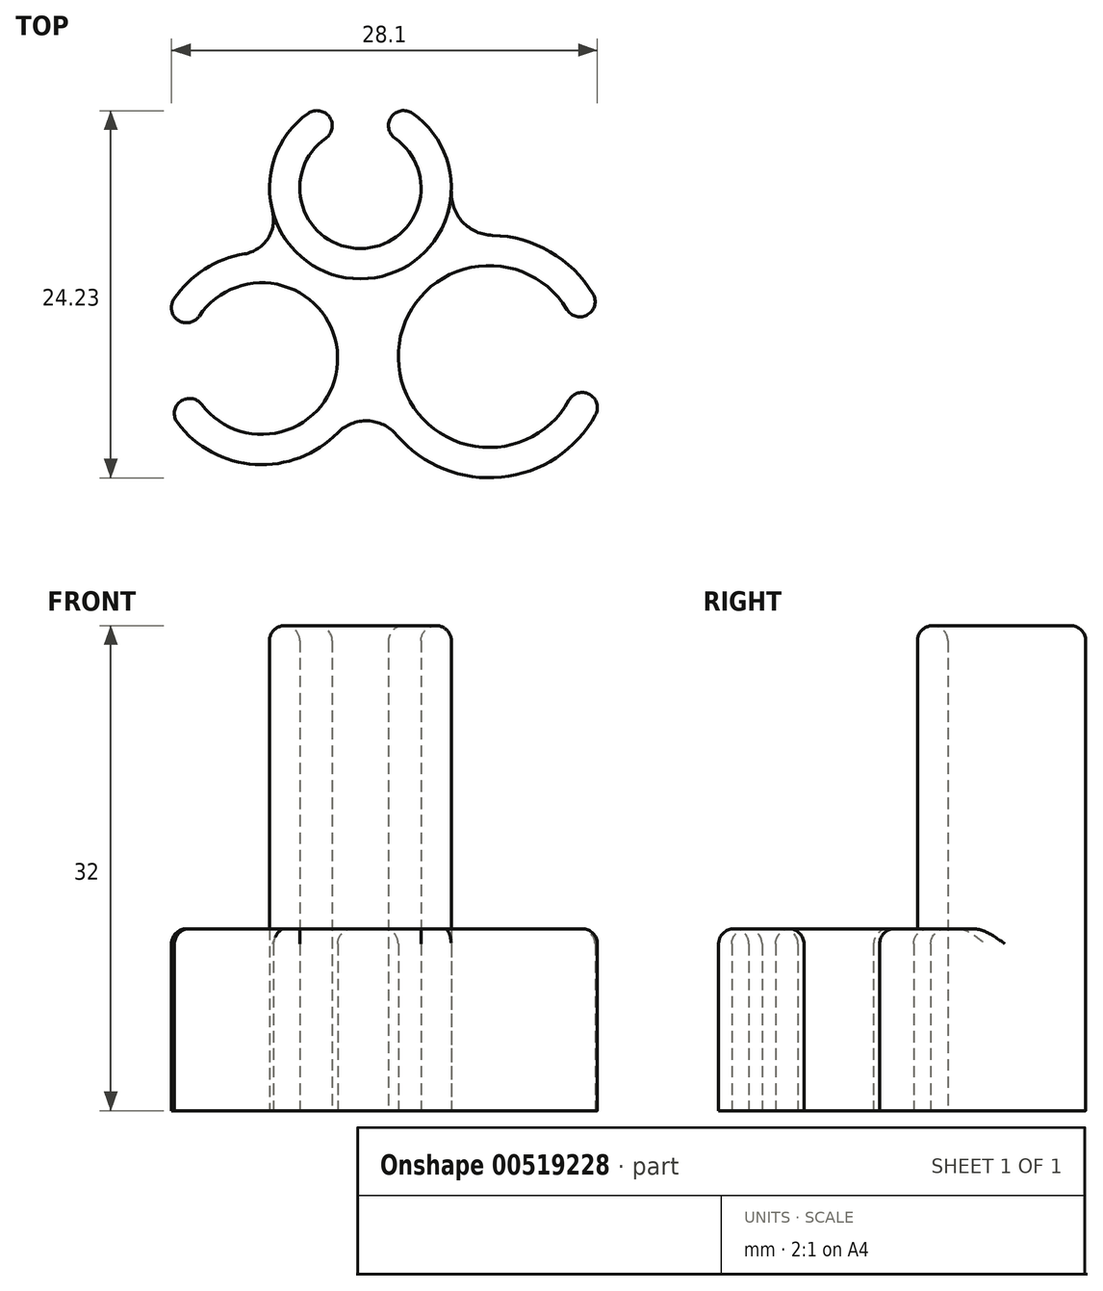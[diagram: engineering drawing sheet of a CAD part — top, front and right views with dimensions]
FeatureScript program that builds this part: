
annotation { "Feature Type Name" : "Feature", "Feature Type Description" : "" }
export const myFeature = defineFeature(function(context is Context, id is Id, definition is map)
    precondition{}
    {
        {
            var Q0;
            Q0=qCreatedBy(makeId("Top.planeOp"),FACE);
            var sketch = newSketch(context, id + "F0", { "sketchPlane" : qUnion([Q0])});
            skArc(sketch, "E0", {"start": v(-6.8, -8.16) * mm, "mid": v(-10.15, -9.7) * mm, "end": v(-12.25, -12.73) * mm});
            skArc(sketch, "E1", {"start": v(3.25, -20.1) * mm, "mid": v(10.96, -22.77) * mm, "end": v(17, -17.28) * mm});
            skArc(sketch, "E2", {"start": v(6.84, -4.04) * mm, "mid": v(5.77, -0.38) * mm, "end": v(2.7, 1.9) * mm});
            skArc(sketch, "E3", {"start": v(14.75, -12.32) * mm, "mid": v(3.35, -15.07) * mm, "end": v(14.86, -17.31) * mm});
            skArc(sketch, "E4", {"start": v(-1.01, -0.27) * mm, "mid": v(0.85, -7.81) * mm, "end": v(2.7, -0.27) * mm});
            skArc(sketch, "E5", {"start": v(-9.9, -17.7) * mm, "mid": v(-0.65, -14.92) * mm, "end": v(-10.06, -12.7) * mm});
            skArc(sketch, "E6", {"start": v(6.84, -4.04) * mm, "mid": v(7.6, -6.06) * mm, "end": v(9.56, -6.94) * mm});
            skArc(sketch, "E7", {"start": v(3.25, -20.1) * mm, "mid": v(1.33, -19.18) * mm, "end": v(-0.65, -19.97) * mm});
            skArc(sketch, "E8", {"start": v(-6.8, -8.16) * mm, "mid": v(-5.25, -7.15) * mm, "end": v(-4.96, -5.32) * mm});
            skLineSegment(sketch, "E9", {"start": v(16.9, -12.29) * mm, "end": v(14.75, -12.32) * mm});
            skLineSegment(sketch, "E10", {"start": v(-12.13, -17.73) * mm, "end": v(-9.9, -17.7) * mm});
            skArc(sketch, "E11.trimOffspring", {"start": v(16.9, -12.29) * mm, "mid": v(14.06, -8.47) * mm, "end": v(9.56, -6.94) * mm});
            skArc(sketch, "E12.trimOffspring", {"start": v(-12.13, -17.73) * mm, "mid": v(-7, -21.94) * mm, "end": v(-0.65, -19.97) * mm});
            skPoint(sketch, "E13.start.orphan", {"position": v(20.68, -17.22) * mm});
            skPoint(sketch, "E14.orphan", {"position": v(20.33, -12.23) * mm});
            skLineSegment(sketch, "E15.trimOffspring", {"start": v(-10.06, -12.7) * mm, "end": v(-12.25, -12.73) * mm});
            skLineSegment(sketch, "E16.trimOffspring", {"start": v(14.86, -17.31) * mm, "end": v(17, -17.28) * mm});
            skLineSegment(sketch, "E17.left", {"start": v(-1.01, 1.9) * mm, "end": v(-1.01, -0.27) * mm});
            skLineSegment(sketch, "E17.right", {"start": v(2.7, 1.9) * mm, "end": v(2.7, -0.27) * mm});
            skArc(sketch, "E18.trimOffspring", {"start": v(-1.01, 1.9) * mm, "mid": v(-4.42, -0.93) * mm, "end": v(-4.96, -5.32) * mm});
            skPoint(sketch, "E17.top.end.orphan", {"position": v(2.7, -3.81) * mm});
            skPoint(sketch, "E19.orphan", {"position": v(-1.01, 3.52) * mm});
            skPoint(sketch, "E20.orphan", {"position": v(2.7, 3.52) * mm});
            skSolve(sketch);
        }
        {
            var Q0;
            Q0=qSketchRegion(id+"F0",true);
            extrude(context, id + "F1", {"entities" : qUnion([Q0]), "depth" : 12 * mm});
        }
        {
            var Q0;
            Q0=makeQuery(id+"F1.opExtrude","CAP_FACE",FACE,{"disambiguationData":[OSD([sQuery(id+"F0.wireOp",EDGE,"E0"),sQuery(id+"F0.wireOp",EDGE,"E1"),sQuery(id+"F0.wireOp",EDGE,"E2"),sQuery(id+"F0.wireOp",EDGE,"E3"),sQuery(id+"F0.wireOp",EDGE,"E4"),sQuery(id+"F0.wireOp",EDGE,"E5"),sQuery(id+"F0.wireOp",EDGE,"E6"),sQuery(id+"F0.wireOp",EDGE,"E7"),sQuery(id+"F0.wireOp",EDGE,"E8"),sQuery(id+"F0.wireOp",EDGE,"E9"),sQuery(id+"F0.wireOp",EDGE,"E10"),sQuery(id+"F0.wireOp",EDGE,"E11.trimOffspring"),sQuery(id+"F0.wireOp",EDGE,"E12.trimOffspring"),sQuery(id+"F0.wireOp",EDGE,"E15.trimOffspring"),sQuery(id+"F0.wireOp",EDGE,"E16.trimOffspring"),sQuery(id+"F0.wireOp",EDGE,"E17.left"),sQuery(id+"F0.wireOp",EDGE,"E17.right"),sQuery(id+"F0.wireOp",EDGE,"E18.trimOffspring")])],"isStart":false});
            var sketch = newSketch(context, id + "F2", { "sketchPlane" : qUnion([Q0])});
            skArc(sketch, "E21", {"start": v(-1.01, 1.9) * mm, "mid": v(0.85, -9.81) * mm, "end": v(2.7, 1.9) * mm});
            skArc(sketch, "E22", {"start": v(-1.01, -0.27) * mm, "mid": v(0.85, -7.81) * mm, "end": v(2.7, -0.27) * mm});
            skLineSegment(sketch, "E23", {"start": v(-1.01, -0.27) * mm, "end": v(-1.01, 1.9) * mm});
            skLineSegment(sketch, "E24", {"start": v(2.7, -0.27) * mm, "end": v(2.7, 1.9) * mm});
            skSolve(sketch);
        }
        {
            var Q0;
            Q0=makeQuery(id+"F2.imprint","IMPRINT",FACE,{"disambiguationData":[TD([[makeQuery(id+"F2.imprint","IMPRINT",EDGE,{"derivedFrom":sQuery(id+"F2.wireOp",EDGE,"E22")}),-1.0]])]});
            extrude(context, id + "F3", {"entities" : qUnion([Q0]), "operationType" : NewBodyOperationType.ADD, "depth" : 20 * mm});
        }
        {
            var Q0;
            Q0=makeQuery(id+"F3.boolean.opBoolean","MERGE",EDGE,{"derivedFrom":[makeQuery(id+"F1.opExtrude","SWEPT_EDGE",EDGE,{"disambiguationData":[OSD([sQuery(id+"F0.wireOp",EDGE,"E2"),sQuery(id+"F0.wireOp",EDGE,"E17.right")])]}),makeQuery(id+"F3.opExtrude","SWEPT_EDGE",EDGE,{"disambiguationData":[OSD([sQuery(id+"F2.wireOp",EDGE,"E21"),sQuery(id+"F2.wireOp",EDGE,"E24")])]})]});
            var Q1;
            Q1=makeQuery(id+"F3.boolean.opBoolean","MERGE",EDGE,{"derivedFrom":[makeQuery(id+"F1.opExtrude","SWEPT_EDGE",EDGE,{"disambiguationData":[OSD([sQuery(id+"F0.wireOp",EDGE,"E17.left"),sQuery(id+"F0.wireOp",EDGE,"E18.trimOffspring")])]}),makeQuery(id+"F3.opExtrude","SWEPT_EDGE",EDGE,{"disambiguationData":[OSD([sQuery(id+"F2.wireOp",EDGE,"E21"),sQuery(id+"F2.wireOp",EDGE,"E23")])]})]});
            var Q2;
            Q2=makeQuery(id+"F1.opExtrude","SWEPT_EDGE",EDGE,{"disambiguationData":[OSD([sQuery(id+"F0.wireOp",EDGE,"E10"),sQuery(id+"F0.wireOp",EDGE,"E12.trimOffspring")])]});
            var Q3;
            Q3=makeQuery(id+"F1.opExtrude","SWEPT_EDGE",EDGE,{"disambiguationData":[OSD([sQuery(id+"F0.wireOp",EDGE,"E0"),sQuery(id+"F0.wireOp",EDGE,"E15.trimOffspring")])]});
            fillet(context, id + "F4", {"entities" : qUnion([Q0, Q1, Q2, Q3]), "radius" : 1 * mm, "tangentPropagation" : true, "allowEdgeOverflow" : false});
        }
        {
            var Q0;
            Q0=makeQuery(id+"F3.boolean.opBoolean","MERGE",EDGE,{"derivedFrom":[makeQuery(id+"F1.opExtrude","SWEPT_EDGE",EDGE,{"disambiguationData":[OSD([sQuery(id+"F0.wireOp",EDGE,"E4"),sQuery(id+"F0.wireOp",EDGE,"E17.left")])]}),makeQuery(id+"F3.opExtrude","SWEPT_EDGE",EDGE,{"disambiguationData":[OSD([sQuery(id+"F2.wireOp",EDGE,"E22"),sQuery(id+"F2.wireOp",EDGE,"E23")])]})]});
            var Q1;
            Q1=makeQuery(id+"F1.opExtrude","SWEPT_EDGE",EDGE,{"disambiguationData":[OSD([sQuery(id+"F0.wireOp",EDGE,"E5"),sQuery(id+"F0.wireOp",EDGE,"E15.trimOffspring")])]});
            var Q2;
            Q2=makeQuery(id+"F1.opExtrude","SWEPT_EDGE",EDGE,{"disambiguationData":[OSD([sQuery(id+"F0.wireOp",EDGE,"E5"),sQuery(id+"F0.wireOp",EDGE,"E10")])]});
            fillet(context, id + "F5", {"entities" : qUnion([Q0, Q1, Q2]), "radius" : 1 * mm, "tangentPropagation" : true, "allowEdgeOverflow" : false});
        }
        {
            var Q0;
            Q0=makeQuery(id+"F3.boolean.opBoolean","MERGE",EDGE,{"derivedFrom":[makeQuery(id+"F1.opExtrude","SWEPT_EDGE",EDGE,{"disambiguationData":[OSD([sQuery(id+"F0.wireOp",EDGE,"E4"),sQuery(id+"F0.wireOp",EDGE,"E17.right")])]}),makeQuery(id+"F3.opExtrude","SWEPT_EDGE",EDGE,{"disambiguationData":[OSD([sQuery(id+"F2.wireOp",EDGE,"E22"),sQuery(id+"F2.wireOp",EDGE,"E24")])]})]});
            fillet(context, id + "F6", {"entities" : qUnion([Q0]), "radius" : 1 * mm, "tangentPropagation" : true, "allowEdgeOverflow" : false});
        }
        {
            var Q0;
            Q0=makeQuery(id+"F1.opExtrude","SWEPT_EDGE",EDGE,{"disambiguationData":[OSD([sQuery(id+"F0.wireOp",EDGE,"E1"),sQuery(id+"F0.wireOp",EDGE,"E16.trimOffspring")])]});
            var Q1;
            Q1=makeQuery(id+"F1.opExtrude","SWEPT_EDGE",EDGE,{"disambiguationData":[OSD([sQuery(id+"F0.wireOp",EDGE,"E9"),sQuery(id+"F0.wireOp",EDGE,"E11.trimOffspring")])]});
            var Q2;
            Q2=makeQuery(id+"F1.opExtrude","SWEPT_EDGE",EDGE,{"disambiguationData":[OSD([sQuery(id+"F0.wireOp",EDGE,"E3"),sQuery(id+"F0.wireOp",EDGE,"E9")])]});
            var Q3;
            Q3=makeQuery(id+"F1.opExtrude","SWEPT_EDGE",EDGE,{"disambiguationData":[OSD([sQuery(id+"F0.wireOp",EDGE,"E3"),sQuery(id+"F0.wireOp",EDGE,"E16.trimOffspring")])]});
            fillet(context, id + "F7", {"entities" : qUnion([Q0, Q1, Q2, Q3]), "radius" : 1 * mm, "tangentPropagation" : true, "allowEdgeOverflow" : false});
        }
        {
            var Q0;
            Q0=makeQuery(id+"F1.opExtrude","CAP_EDGE",EDGE,{"disambiguationData":[OSD([sQuery(id+"F0.wireOp",EDGE,"E3")])],"isStart":false});
            var Q1;
            Q1=makeQuery(id+"F1.opExtrude","CAP_EDGE",EDGE,{"disambiguationData":[OSD([sQuery(id+"F0.wireOp",EDGE,"E5")])],"isStart":false});
            var Q2;
            Q2=makeQuery(id+"F3.opExtrude","CAP_EDGE",EDGE,{"disambiguationData":[OSD([sQuery(id+"F2.wireOp",EDGE,"E22")])],"isStart":false});
            fillet(context, id + "F8", {"entities" : qUnion([Q0, Q1, Q2]), "radius" : 1 * mm, "tangentPropagation" : true, "allowEdgeOverflow" : false});
        }
    });
